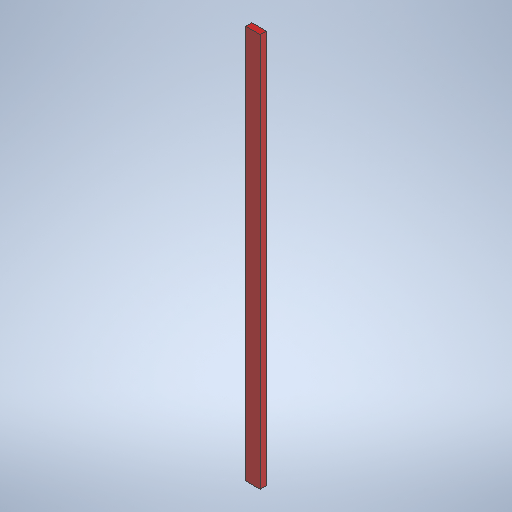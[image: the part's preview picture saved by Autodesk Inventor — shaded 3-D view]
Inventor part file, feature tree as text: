
AUTODESK INVENTOR PART (.ipt)
format: ipt  version: 2025.1 (Build 291241020, 241B)  size: 252,928 bytes
history: native  units: in
note: dims shown in document units (in); Inventor stores cm internally (conversion verified against a paired STEP export)
features: extrude x1, sketch x1, other x1
ambient origin geometry x8: Origin, YZ Plane, XZ Plane, XY Plane, X Axis, Y Axis, Z Axis, Center Point
bodies: Solid1 (feature_tree)
feature tree (3):
  extrude  "Extrusion1"  Depth=3.5in
  sketch  "Sketch1"  dims[d0=1.5in d1=3.5in d2=96.0in d3=0.0in]
  other  "Finish1"
